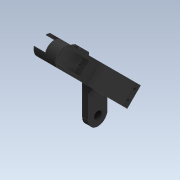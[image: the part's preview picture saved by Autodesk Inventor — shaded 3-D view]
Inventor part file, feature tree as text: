
AUTODESK INVENTOR PART (.ipt)
format: ipt  version: 2020 (Build 240168000, 168)  size: 569,344 bytes
history: native  units: in
note: dims shown in document units (in); Inventor stores cm internally (conversion verified against a paired STEP export)
features: sketch x26, other x8, extrude x5, projected_geometry x5, chamfer x4, plane x4
ambient origin geometry x8: Origin, YZ Plane, XZ Plane, XY Plane, X Axis, Y Axis, Z Axis, Center Point
bodies: Solid2 (feature_tree), Solid3 (feature_tree), Solid1 (feature_tree), Solid4 (feature_tree), Solid5 (feature_tree)
feature tree (52):
  other  "LegMidBot.ipt"
  chamfer  "Chamfer1"  Distance=0.0787in Angle=45.0deg
  chamfer  "Chamfer2"  Distance=0.0787in Angle=45.0deg
  chamfer  "Chamfer3"  Distance=0.1969in Angle=45.0deg
  chamfer  "Chamfer4"  Distance=0.0787in Angle=45.0deg
  extrude  "Extrusion4"  Depth=0.4813in TaperAngle=0.0deg
  extrude  "Extrusion5"  Depth=0.0059in
  extrude  "Extrusion6"  Depth=0.3937in TaperAngle=0.0deg
  extrude  "Extrusion7"  Depth=0.0039in
  extrude  "Extrusion8"  Depth=0.3937in TaperAngle=0.0deg
  other  "Solid1::LegMidBot.ipt"
  other  "Solid2::LegMidBot.ipt"
  other  "Solid3::LegMidBot.ipt"
  other  "Solid4::LegMidBot.ipt"
  other  "Solid5::LegMidBot.ipt"
  other  "Solid6::LegMidBot.ipt"
  other  "TaggingFeature1"
  sketch  "Sketch1"  dims[d0=0.3937in d12=0.0787in d13=0.0787in d14=45.0deg d15=0.0787in d16=0.0787in d17=45.0deg d18=0.1969in d19=0.0787in d20=45.0deg d21=0.0787in d22=0.0787in d23=45.0deg]
  sketch  "Sketch2"  dims[d24=0.1147in d25=0.4813in d26=0.0in]
  sketch  "Sketch3"  dims[d27=0.0059in d28=0.0059in]
  sketch  "Sketch4"  dims[d29=0.0059in d30=0.3937in d31=0.0in]
  sketch  "Sketch5"  dims[d32=0.0039in d33=0.0039in]
  sketch  "Sketch12"  dims[d34=0.3937in d35=0.0in d36=0.3937in d37=0.0in]
  sketch  "Sketch14"  dims[d38=0.3937in d39=0.0in]
  sketch  "Sketch15"
  sketch  "Sketch16"
  sketch  "Sketch17"
  sketch  "Sketch19"
  sketch  "Sketch22"
  sketch  "Sketch23"
  sketch  "Sketch25"
  sketch  "Sketch26"
  sketch  "Sketch27"
  sketch  "Sketch28"
  sketch  "Sketch32"
  sketch  "Sketch33"
  sketch  "Sketch39"
  sketch  "Sketch40"
  plane  "Work Plane1"
  plane  "Work Plane2"
  plane  "Work Plane3"
  plane  "Work Plane4"
  sketch  "Sketch46"
  projected_geometry  "Projected Loop5"
  sketch  "Sketch47"
  projected_geometry  "Projected Loop6"
  sketch  "Sketch48"
  projected_geometry  "Projected Loop7"
  sketch  "Sketch49"
  projected_geometry  "Projected Loop8"
  projected_geometry  "Projected Loop9"
  sketch  "Sketch50"
